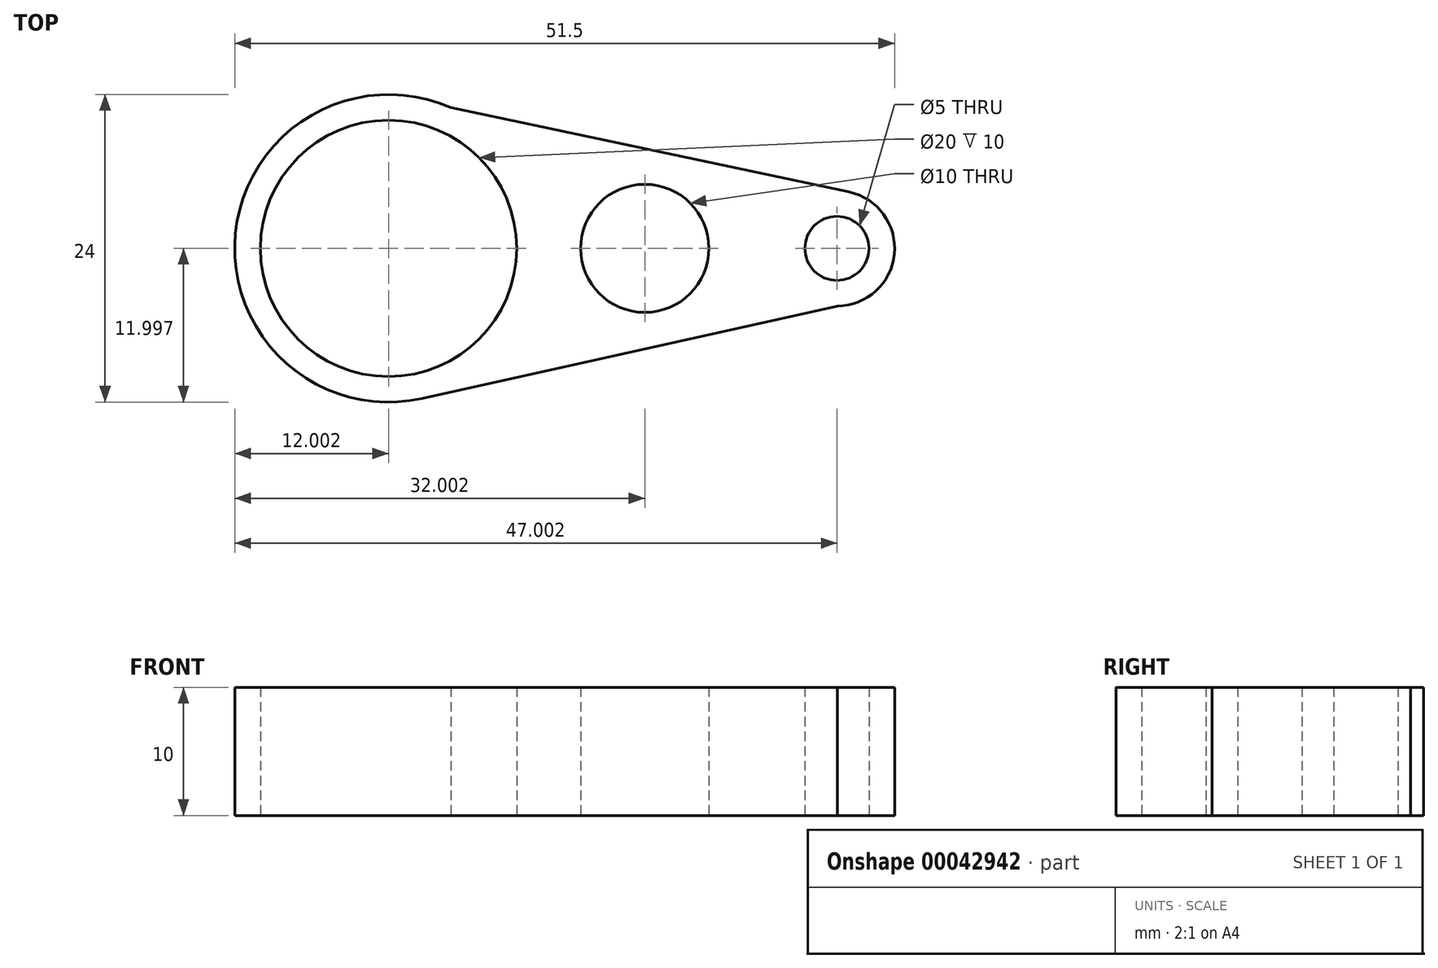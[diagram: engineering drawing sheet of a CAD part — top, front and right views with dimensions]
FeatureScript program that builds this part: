
annotation { "Feature Type Name" : "Feature", "Feature Type Description" : "" }
export const myFeature = defineFeature(function(context is Context, id is Id, definition is map)
    precondition{}
    {
        {
            var Q0;
            Q0=qCreatedBy(makeId("Top.planeOp"),FACE);
            var sketch = newSketch(context, id + "F0", { "sketchPlane" : qUnion([Q0])});
            skLineSegment(sketch, "E0", {"start": v(21, -4.45) * mm, "end": v(-11.42, -11.67) * mm});
            skLineSegment(sketch, "E1", {"start": v(-9.17, 11.02) * mm, "end": v(21.9, 4.45) * mm});
            skArc(sketch, "E2.0", {"start": v(-9.17, 11.02) * mm, "mid": v(-25.97, 1.23) * mm, "end": v(-11.42, -11.67) * mm});
            skArc(sketch, "E3.0", {"start": v(21, -4.45) * mm, "mid": v(25.45, -0.4) * mm, "end": v(21.9, 4.45) * mm});
            skCircle(sketch, "E4", {"center": v(20.97, 0.05) * mm, "radius": 2.5 * mm});
            skCircle(sketch, "E5", {"center": v(-14.03, 0.05) * mm, "radius": 10 * mm});
            skPoint(sketch, "E6.orphan", {"position": v(-14.03, -12.25) * mm});
            skCircle(sketch, "E7", {"center": v(5.97, 0.05) * mm, "radius": 5 * mm});
            skPoint(sketch, "E8.orphan", {"position": v(-14.03, 12.05) * mm});
            skSolve(sketch);
        }
        {
            var Q0;
            Q0=makeQuery(id+"F0.imprint","IMPRINT",FACE,{"disambiguationData":[TD([[makeQuery(id+"F0.imprint","IMPRINT",EDGE,{"derivedFrom":sQuery(id+"F0.wireOp",EDGE,"E0")}),-1.0]])]});
            extrude(context, id + "F1", {"entities" : qUnion([Q0]), "depth" : 10 * mm});
        }
    });
